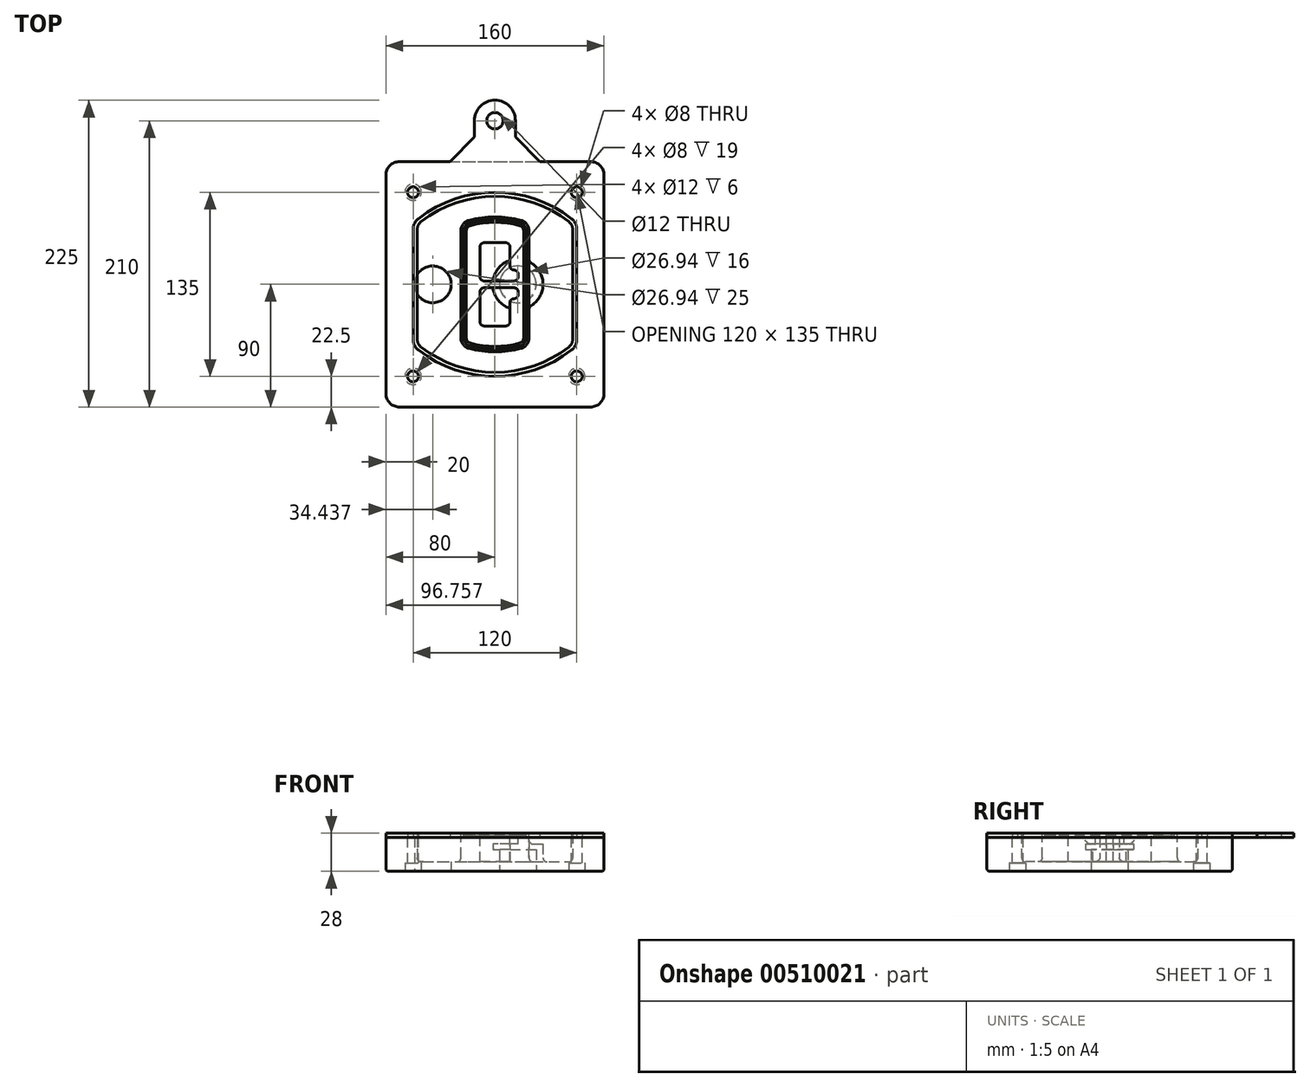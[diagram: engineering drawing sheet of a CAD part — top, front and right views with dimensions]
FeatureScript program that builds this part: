
annotation { "Feature Type Name" : "Feature", "Feature Type Description" : "" }
export const myFeature = defineFeature(function(context is Context, id is Id, definition is map)
    precondition{}
    {
        {
            var Q0;
            Q0=qCreatedBy(makeId("Top.planeOp"),FACE);
            var sketch = newSketch(context, id + "F0", { "sketchPlane" : qUnion([Q0])});
            skPoint(sketch, "E0.rect.middle", {"position": v(0, 0) * mm});
            skLineSegment(sketch, "E1.bottom", {"start": v(-70, -90) * mm, "end": v(70, -90) * mm});
            skLineSegment(sketch, "E1.top", {"start": v(-70, 90) * mm, "end": v(70, 90) * mm});
            skLineSegment(sketch, "E1.left", {"start": v(-80, -80) * mm, "end": v(-80, 80) * mm});
            skLineSegment(sketch, "E1.right", {"start": v(80, -80) * mm, "end": v(80, 80) * mm});
            skLineSegment(sketch, "E2", {"start": v(-80, 90) * mm, "end": v(80, -90) * mm, "construction": true});
            skLineSegment(sketch, "E3", {"start": v(80, 90) * mm, "end": v(-80, -90) * mm, "construction": true});
            skCircle(sketch, "E4", {"center": v(-60, 67.5) * mm, "radius": 4 * mm});
            skCircle(sketch, "E5", {"center": v(60, 67.5) * mm, "radius": 4 * mm});
            skCircle(sketch, "E6", {"center": v(60, -67.5) * mm, "radius": 4 * mm});
            skCircle(sketch, "E7", {"center": v(-60, -67.5) * mm, "radius": 4 * mm});
            skLineSegment(sketch, "E8", {"start": v(-60, 67.5) * mm, "end": v(60, 67.5) * mm, "construction": true});
            skLineSegment(sketch, "E9", {"start": v(60, 67.5) * mm, "end": v(60, -67.5) * mm, "construction": true});
            skLineSegment(sketch, "E10", {"start": v(60, -67.5) * mm, "end": v(-60, -67.5) * mm, "construction": true});
            skLineSegment(sketch, "E11", {"start": v(-60, -67.5) * mm, "end": v(-60, 67.5) * mm, "construction": true});
            skLineSegment(sketch, "E12", {"start": v(-60, 40.3) * mm, "end": v(-60, -40.3) * mm});
            skLineSegment(sketch, "E13", {"start": v(60, 40.3) * mm, "end": v(60, -40.3) * mm});
            skArc(sketch, "E14", {"start": v(56.15, 48.18) * mm, "mid": v(0, 67.5) * mm, "end": v(-56.15, 48.18) * mm});
            skArc(sketch, "E15", {"start": v(-56.15, -48.18) * mm, "mid": v(0, -67.5) * mm, "end": v(56.15, -48.18) * mm});
            skLineSegment(sketch, "E16", {"start": v(-60, 0) * mm, "end": v(60, 0) * mm, "construction": true});
            skPoint(sketch, "E17.visualSharp", {"position": v(-60, -45) * mm});
            skArc(sketch, "E17.filletArc", {"start": v(-60, -40.3) * mm, "mid": v(-58.99, -44.68) * mm, "end": v(-56.15, -48.18) * mm});
            skPoint(sketch, "E18.visualSharp", {"position": v(-60, 45) * mm});
            skArc(sketch, "E18.filletArc", {"start": v(-56.15, 48.18) * mm, "mid": v(-58.99, 44.68) * mm, "end": v(-60, 40.3) * mm});
            skPoint(sketch, "E19.visualSharp", {"position": v(60, 45) * mm});
            skArc(sketch, "E19.filletArc", {"start": v(60, 40.3) * mm, "mid": v(58.99, 44.68) * mm, "end": v(56.15, 48.18) * mm});
            skPoint(sketch, "E20.visualSharp", {"position": v(60, -45) * mm});
            skArc(sketch, "E20.filletArc", {"start": v(56.15, -48.18) * mm, "mid": v(58.99, -44.68) * mm, "end": v(60, -40.3) * mm});
            skPoint(sketch, "E21.visualSharp", {"position": v(-80, 90) * mm});
            skArc(sketch, "E21.filletArc", {"start": v(-70, 90) * mm, "mid": v(-77.07, 87.07) * mm, "end": v(-80, 80) * mm});
            skPoint(sketch, "E22.visualSharp", {"position": v(80, 90) * mm});
            skArc(sketch, "E22.filletArc", {"start": v(80, 80) * mm, "mid": v(77.07, 87.07) * mm, "end": v(70, 90) * mm});
            skPoint(sketch, "E23.visualSharp", {"position": v(80, -90) * mm});
            skArc(sketch, "E23.filletArc", {"start": v(70, -90) * mm, "mid": v(77.07, -87.07) * mm, "end": v(80, -80) * mm});
            skPoint(sketch, "E24.visualSharp", {"position": v(-80, -90) * mm});
            skArc(sketch, "E24.filletArc", {"start": v(-80, -80) * mm, "mid": v(-77.07, -87.07) * mm, "end": v(-70, -90) * mm});
            skArc(sketch, "E25.0", {"start": v(57, 40.3) * mm, "mid": v(56.3, 43.36) * mm, "end": v(54.3, 45.81) * mm});
            skLineSegment(sketch, "E25.1", {"start": v(57, 40.3) * mm, "end": v(57, -40.3) * mm});
            skArc(sketch, "E25.2", {"start": v(54.3, -45.81) * mm, "mid": v(56.3, -43.36) * mm, "end": v(57, -40.3) * mm});
            skArc(sketch, "E25.3", {"start": v(-54.3, -45.81) * mm, "mid": v(0, -64.5) * mm, "end": v(54.3, -45.81) * mm});
            skArc(sketch, "E25.4", {"start": v(-57, -40.3) * mm, "mid": v(-56.3, -43.36) * mm, "end": v(-54.3, -45.81) * mm});
            skArc(sketch, "E25.5", {"start": v(54.3, 45.81) * mm, "mid": v(0, 64.5) * mm, "end": v(-54.3, 45.81) * mm});
            skLineSegment(sketch, "E25.6", {"start": v(-57, 40.3) * mm, "end": v(-57, -40.3) * mm});
            skArc(sketch, "E25.7", {"start": v(-54.3, 45.81) * mm, "mid": v(-56.3, 43.36) * mm, "end": v(-57, 40.3) * mm});
            skArc(sketch, "E26.0", {"start": v(-58.62, 51.33) * mm, "mid": v(-62.58, 46.43) * mm, "end": v(-64, 40.3) * mm});
            skArc(sketch, "E26.1", {"start": v(58.62, 51.33) * mm, "mid": v(0, 71.5) * mm, "end": v(-58.62, 51.33) * mm});
            skArc(sketch, "E26.2", {"start": v(64, 40.3) * mm, "mid": v(62.58, 46.43) * mm, "end": v(58.62, 51.33) * mm});
            skLineSegment(sketch, "E26.3", {"start": v(64, 40.3) * mm, "end": v(64, -40.3) * mm});
            skArc(sketch, "E26.4", {"start": v(58.62, -51.33) * mm, "mid": v(62.58, -46.43) * mm, "end": v(64, -40.3) * mm});
            skLineSegment(sketch, "E26.5", {"start": v(-64, 40.3) * mm, "end": v(-64, -40.3) * mm});
            skArc(sketch, "E26.6", {"start": v(-58.62, -51.33) * mm, "mid": v(0, -71.5) * mm, "end": v(58.62, -51.33) * mm});
            skArc(sketch, "E26.7", {"start": v(-64, -40.3) * mm, "mid": v(-62.58, -46.43) * mm, "end": v(-58.62, -51.33) * mm});
            skSolve(sketch);
        }
        {
            var Q0;
            Q0=makeQuery(id+"F0.imprint","IMPRINT",FACE,{"disambiguationData":[TD([[makeQuery(id+"F0.imprint","IMPRINT",EDGE,{"derivedFrom":sQuery(id+"F0.wireOp",EDGE,"E1.bottom")}),1.0]])]});
            var Q1;
            Q1=makeQuery(id+"F0.imprint","IMPRINT",FACE,{"disambiguationData":[TD([[makeQuery(id+"F0.imprint","IMPRINT",EDGE,{"derivedFrom":sQuery(id+"F0.wireOp",EDGE,"E12")}),1.0]])]});
            var Q2;
            Q2=makeQuery(id+"F0.imprint","IMPRINT",FACE,{"disambiguationData":[TD([[makeQuery(id+"F0.imprint","IMPRINT",EDGE,{"derivedFrom":sQuery(id+"F0.wireOp",EDGE,"E25.0")}),1.0]])]});
            var Q3;
            Q3=makeQuery(id+"F0.imprint","IMPRINT",FACE,{"disambiguationData":[TD([[makeQuery(id+"F0.imprint","IMPRINT",EDGE,{"derivedFrom":sQuery(id+"F0.wireOp",EDGE,"E12")}),-1.0]])]});
            extrude(context, id + "F1", {"entities" : qUnion([Q0, Q1, Q2, Q3]), "oppositeDirection" : true, "depth" : 25 * mm});
        }
        {
            var Q0;
            Q0=makeQuery(id+"F0.imprint","IMPRINT",FACE,{"disambiguationData":[TD([[makeQuery(id+"F0.imprint","IMPRINT",EDGE,{"derivedFrom":sQuery(id+"F0.wireOp",EDGE,"E12")}),1.0]])]});
            extrude(context, id + "F2", {"entities" : qUnion([Q0]), "operationType" : NewBodyOperationType.ADD, "depth" : 3 * mm});
        }
        {
            var Q0;
            Q0=makeQuery(id+"F0.imprint","IMPRINT",FACE,{"disambiguationData":[TD([[makeQuery(id+"F0.imprint","IMPRINT",EDGE,{"derivedFrom":sQuery(id+"F0.wireOp",EDGE,"E25.0")}),1.0]])]});
            extrude(context, id + "F3", {"entities" : qUnion([Q0]), "operationType" : NewBodyOperationType.REMOVE, "oppositeDirection" : true, "depth" : 18 * mm});
        }
        {
            var Q0;
            Q0=makeQuery(id+"F2.opExtrude","CAP_FACE",FACE,{"disambiguationData":[OSD([sQuery(id+"F0.wireOp",EDGE,"E12"),sQuery(id+"F0.wireOp",EDGE,"E13"),sQuery(id+"F0.wireOp",EDGE,"E14"),sQuery(id+"F0.wireOp",EDGE,"E15"),sQuery(id+"F0.wireOp",EDGE,"E17.filletArc"),sQuery(id+"F0.wireOp",EDGE,"E18.filletArc"),sQuery(id+"F0.wireOp",EDGE,"E19.filletArc"),sQuery(id+"F0.wireOp",EDGE,"E20.filletArc"),sQuery(id+"F0.wireOp",EDGE,"E25.0"),sQuery(id+"F0.wireOp",EDGE,"E25.1"),sQuery(id+"F0.wireOp",EDGE,"E25.2"),sQuery(id+"F0.wireOp",EDGE,"E25.3"),sQuery(id+"F0.wireOp",EDGE,"E25.4"),sQuery(id+"F0.wireOp",EDGE,"E25.5"),sQuery(id+"F0.wireOp",EDGE,"E25.6"),sQuery(id+"F0.wireOp",EDGE,"E25.7")])],"isStart":false});
            var sketch = newSketch(context, id + "F4", { "sketchPlane" : qUnion([Q0])});
            skArc(sketch, "E27.0", {"start": v(-19.08, -46.97) * mm, "mid": v(0, -49.5) * mm, "end": v(19.08, -46.97) * mm});
            skArc(sketch, "E28.0", {"start": v(19.08, 46.97) * mm, "mid": v(0, 49.5) * mm, "end": v(-19.08, 46.97) * mm});
            skLineSegment(sketch, "E29", {"start": v(-25, 39.25) * mm, "end": v(-25, -39.25) * mm});
            skLineSegment(sketch, "E30", {"start": v(25, 39.25) * mm, "end": v(25, -39.25) * mm});
            skLineSegment(sketch, "E31", {"start": v(-25, 45.1) * mm, "end": v(25, 45.1) * mm, "construction": true});
            skLineSegment(sketch, "E32", {"start": v(-25, -45.1) * mm, "end": v(25, -45.1) * mm, "construction": true});
            skPoint(sketch, "E33.visualSharp", {"position": v(-25, 45.1) * mm});
            skArc(sketch, "E33.filletArc", {"start": v(-19.08, 46.97) * mm, "mid": v(-23.35, 44.11) * mm, "end": v(-25, 39.25) * mm});
            skPoint(sketch, "E34.visualSharp", {"position": v(25, 45.1) * mm});
            skArc(sketch, "E34.filletArc", {"start": v(25, 39.25) * mm, "mid": v(23.35, 44.11) * mm, "end": v(19.08, 46.97) * mm});
            skPoint(sketch, "E35.visualSharp", {"position": v(25, -45.1) * mm});
            skArc(sketch, "E35.filletArc", {"start": v(19.08, -46.97) * mm, "mid": v(23.35, -44.11) * mm, "end": v(25, -39.25) * mm});
            skPoint(sketch, "E36.visualSharp", {"position": v(-25, -45.1) * mm});
            skArc(sketch, "E36.filletArc", {"start": v(-25, -39.25) * mm, "mid": v(-23.35, -44.11) * mm, "end": v(-19.08, -46.97) * mm});
            skArc(sketch, "E37.0", {"start": v(54.3, 45.81) * mm, "mid": v(0, 64.5) * mm, "end": v(-54.3, 45.81) * mm});
            skArc(sketch, "E37.1", {"start": v(-54.3, 45.81) * mm, "mid": v(-56.3, 43.36) * mm, "end": v(-57, 40.3) * mm});
            skLineSegment(sketch, "E37.2", {"start": v(-57, 40.3) * mm, "end": v(-57, -40.3) * mm});
            skArc(sketch, "E37.3", {"start": v(-57, -40.3) * mm, "mid": v(-56.3, -43.36) * mm, "end": v(-54.3, -45.81) * mm});
            skArc(sketch, "E37.4", {"start": v(-54.3, -45.81) * mm, "mid": v(0, -64.5) * mm, "end": v(54.3, -45.81) * mm});
            skArc(sketch, "E37.5", {"start": v(54.3, -45.81) * mm, "mid": v(56.3, -43.36) * mm, "end": v(57, -40.3) * mm});
            skLineSegment(sketch, "E37.6", {"start": v(57, 40.3) * mm, "end": v(57, -40.3) * mm});
            skArc(sketch, "E37.7", {"start": v(57, 40.3) * mm, "mid": v(56.3, 43.36) * mm, "end": v(54.3, 45.81) * mm});
            skLineSegment(sketch, "E38.0", {"start": v(23, 39.25) * mm, "end": v(23, -39.25) * mm});
            skArc(sketch, "E38.1", {"start": v(18.56, -45.04) * mm, "mid": v(21.76, -42.9) * mm, "end": v(23, -39.25) * mm});
            skArc(sketch, "E38.2", {"start": v(-18.56, -45.04) * mm, "mid": v(0, -47.5) * mm, "end": v(18.56, -45.04) * mm});
            skArc(sketch, "E38.3", {"start": v(-23, -39.25) * mm, "mid": v(-21.76, -42.9) * mm, "end": v(-18.56, -45.04) * mm});
            skLineSegment(sketch, "E38.4", {"start": v(-23, 39.25) * mm, "end": v(-23, -39.25) * mm});
            skArc(sketch, "E38.5", {"start": v(23, 39.25) * mm, "mid": v(21.76, 42.9) * mm, "end": v(18.56, 45.04) * mm});
            skArc(sketch, "E38.6", {"start": v(-18.56, 45.04) * mm, "mid": v(-21.76, 42.9) * mm, "end": v(-23, 39.25) * mm});
            skArc(sketch, "E38.7", {"start": v(18.56, 45.04) * mm, "mid": v(0, 47.5) * mm, "end": v(-18.56, 45.04) * mm});
            skArc(sketch, "E39.0", {"start": v(21, 39.25) * mm, "mid": v(20.18, 41.68) * mm, "end": v(18.04, 43.1) * mm});
            skLineSegment(sketch, "E39.1", {"start": v(21, 39.25) * mm, "end": v(21, -39.25) * mm});
            skArc(sketch, "E39.2", {"start": v(18.04, -43.1) * mm, "mid": v(20.18, -41.68) * mm, "end": v(21, -39.25) * mm});
            skArc(sketch, "E39.3", {"start": v(-18.04, -43.1) * mm, "mid": v(0, -45.5) * mm, "end": v(18.04, -43.1) * mm});
            skArc(sketch, "E39.4", {"start": v(-21, -39.25) * mm, "mid": v(-20.18, -41.68) * mm, "end": v(-18.04, -43.1) * mm});
            skArc(sketch, "E39.5", {"start": v(18.04, 43.1) * mm, "mid": v(0, 45.5) * mm, "end": v(-18.04, 43.1) * mm});
            skLineSegment(sketch, "E39.6", {"start": v(-21, 39.25) * mm, "end": v(-21, -39.25) * mm});
            skArc(sketch, "E39.7", {"start": v(-18.04, 43.1) * mm, "mid": v(-20.18, 41.68) * mm, "end": v(-21, 39.25) * mm});
            skLineSegment(sketch, "E40", {"start": v(-25, 0) * mm, "end": v(25, 0) * mm, "construction": true});
            skLineSegment(sketch, "E41", {"start": v(-11, 5.5) * mm, "end": v(-11, 27.5) * mm});
            skLineSegment(sketch, "E42", {"start": v(-8, 30.5) * mm, "end": v(8, 30.5) * mm});
            skLineSegment(sketch, "E43", {"start": v(11, 27.5) * mm, "end": v(11, 13.5) * mm});
            skLineSegment(sketch, "E44", {"start": v(14, 10.5) * mm, "end": v(14, 10.5) * mm});
            skLineSegment(sketch, "E45", {"start": v(17, 7.5) * mm, "end": v(17, 5.5) * mm});
            skLineSegment(sketch, "E46", {"start": v(14, 2.5) * mm, "end": v(-8, 2.5) * mm});
            skPoint(sketch, "E47.visualSharp", {"position": v(-11, 30.5) * mm});
            skArc(sketch, "E47.filletArc", {"start": v(-8, 30.5) * mm, "mid": v(-10.12, 29.62) * mm, "end": v(-11, 27.5) * mm});
            skPoint(sketch, "E48.visualSharp", {"position": v(11, 30.5) * mm});
            skArc(sketch, "E48.filletArc", {"start": v(11, 27.5) * mm, "mid": v(10.12, 29.62) * mm, "end": v(8, 30.5) * mm});
            skPoint(sketch, "E49.visualSharp", {"position": v(11, 10.5) * mm});
            skArc(sketch, "E49.filletArc", {"start": v(11, 13.5) * mm, "mid": v(11.88, 11.38) * mm, "end": v(14, 10.5) * mm});
            skPoint(sketch, "E50.visualSharp", {"position": v(17, 10.5) * mm});
            skArc(sketch, "E50.filletArc", {"start": v(17, 7.5) * mm, "mid": v(16.12, 9.62) * mm, "end": v(14, 10.5) * mm});
            skPoint(sketch, "E51.visualSharp", {"position": v(17, 2.5) * mm});
            skArc(sketch, "E51.filletArc", {"start": v(14, 2.5) * mm, "mid": v(16.12, 3.38) * mm, "end": v(17, 5.5) * mm});
            skPoint(sketch, "E52.visualSharp", {"position": v(-11, 2.5) * mm});
            skArc(sketch, "E52.filletArc", {"start": v(-11, 5.5) * mm, "mid": v(-10.12, 3.38) * mm, "end": v(-8, 2.5) * mm});
            skLineSegment(sketch, "E53.0.MirrorCS", {"start": v(14, -2.5) * mm, "end": v(-8, -2.5) * mm});
            skArc(sketch, "E54.0.MirrorCS", {"start": v(-11, -5.5) * mm, "mid": v(-10.12, -3.38) * mm, "end": v(-8, -2.5) * mm});
            skLineSegment(sketch, "E55.0.MirrorCS", {"start": v(-11, -5.5) * mm, "end": v(-11, -27.5) * mm});
            skArc(sketch, "E56.0.MirrorCS", {"start": v(-8, -30.5) * mm, "mid": v(-10.12, -29.62) * mm, "end": v(-11, -27.5) * mm});
            skLineSegment(sketch, "E57.0.MirrorCS", {"start": v(-8, -30.5) * mm, "end": v(8, -30.5) * mm});
            skArc(sketch, "E58.0.MirrorCS", {"start": v(11, -27.5) * mm, "mid": v(10.12, -29.62) * mm, "end": v(8, -30.5) * mm});
            skLineSegment(sketch, "E59.0.MirrorCS", {"start": v(11, -27.5) * mm, "end": v(11, -13.5) * mm});
            skArc(sketch, "E60.0.MirrorCS", {"start": v(11, -13.5) * mm, "mid": v(11.88, -11.38) * mm, "end": v(14, -10.5) * mm});
            skArc(sketch, "E61.0.MirrorCS", {"start": v(17, -7.5) * mm, "mid": v(16.12, -9.62) * mm, "end": v(14, -10.5) * mm});
            skLineSegment(sketch, "E62.0.MirrorCS", {"start": v(17, -7.5) * mm, "end": v(17, -5.5) * mm});
            skArc(sketch, "E63.0.MirrorCS", {"start": v(14, -2.5) * mm, "mid": v(16.12, -3.38) * mm, "end": v(17, -5.5) * mm});
            skSolve(sketch);
        }
        {
            var Q0;
            Q0=makeQuery(id+"F4.imprint","IMPRINT",FACE,{"disambiguationData":[TD([[makeQuery(id+"F4.imprint","IMPRINT",EDGE,{"derivedFrom":sQuery(id+"F4.wireOp",EDGE,"E27.0")}),1.0]])]});
            var Q1;
            Q1=makeQuery(id+"F4.imprint","IMPRINT",FACE,{"disambiguationData":[TD([[makeQuery(id+"F4.imprint","IMPRINT",EDGE,{"derivedFrom":sQuery(id+"F4.wireOp",EDGE,"E38.0")}),-1.0]])]});
            var Q2;
            Q2=makeQuery(id+"F4.imprint","IMPRINT",FACE,{"disambiguationData":[TD([[makeQuery(id+"F4.imprint","IMPRINT",EDGE,{"derivedFrom":sQuery(id+"F4.wireOp",EDGE,"E39.0")}),1.0]])]});
            extrude(context, id + "F5", {"entities" : qUnion([Q0, Q1, Q2]), "operationType" : NewBodyOperationType.ADD, "endBound" : BoundingType.UP_TO_NEXT, "oppositeDirection" : true, "depth" : 25 * mm});
        }
        {
            var Q0;
            Q0=makeQuery(id+"F4.imprint","IMPRINT",FACE,{"disambiguationData":[TD([[makeQuery(id+"F4.imprint","IMPRINT",EDGE,{"derivedFrom":sQuery(id+"F4.wireOp",EDGE,"E38.0")}),-1.0]])]});
            extrude(context, id + "F6", {"entities" : qUnion([Q0]), "operationType" : NewBodyOperationType.REMOVE, "oppositeDirection" : true, "depth" : 2 * mm});
        }
        {
            var Q0;
            Q0=makeQuery(id+"F1.opExtrude","CAP_FACE",FACE,{"disambiguationData":[OSD([sQuery(id+"F0.wireOp",EDGE,"E1.bottom"),sQuery(id+"F0.wireOp",EDGE,"E1.top"),sQuery(id+"F0.wireOp",EDGE,"E1.left"),sQuery(id+"F0.wireOp",EDGE,"E1.right"),sQuery(id+"F0.wireOp",EDGE,"E4"),sQuery(id+"F0.wireOp",EDGE,"E5"),sQuery(id+"F0.wireOp",EDGE,"E6"),sQuery(id+"F0.wireOp",EDGE,"E7"),sQuery(id+"F0.wireOp",EDGE,"E21.filletArc"),sQuery(id+"F0.wireOp",EDGE,"E22.filletArc"),sQuery(id+"F0.wireOp",EDGE,"E23.filletArc"),sQuery(id+"F0.wireOp",EDGE,"E24.filletArc")])],"isStart":false});
            var sketch = newSketch(context, id + "F7", { "sketchPlane" : qUnion([Q0])});
            skCircle(sketch, "E64", {"center": v(16.76, 0) * mm, "radius": 13.47 * mm});
            skCircle(sketch, "E65", {"center": v(-45.56, 0) * mm, "radius": 13.47 * mm});
            skLineSegment(sketch, "E66", {"start": v(80, 0) * mm, "end": v(-80, 0) * mm});
            skCircle(sketch, "E67", {"center": v(16.76, 0) * mm, "radius": 18.47 * mm});
            skCircle(sketch, "E68", {"center": v(60, -67.5) * mm, "radius": 6 * mm});
            skCircle(sketch, "E69", {"center": v(-60, -67.5) * mm, "radius": 6 * mm});
            skCircle(sketch, "E70", {"center": v(-60, 67.5) * mm, "radius": 6 * mm});
            skCircle(sketch, "E71", {"center": v(60, 67.5) * mm, "radius": 6 * mm});
            skSolve(sketch);
        }
        {
            var Q0;
            {var subQ1=sQuery(id+"F7.wireOp",EDGE,"E66");var subQ4=sQuery(id+"F7.wireOp",EDGE,"E64");var subQ6=makeQuery(id+"F7.imprint","INTERSECT",VERTEX,{"disambiguationData":[OD(0.0)],"derivedFrom":[subQ4,subQ1]});Q0=makeQuery(id+"F7.imprint","IMPRINT",FACE,{"disambiguationData":[TD([[makeQuery(id+"F7.imprint","IMPRINT",EDGE,{"disambiguationData":[TD([[subQ6,-1.0]])],"derivedFrom":subQ4}),-1.0]])]});}
            var Q1;
            {var subQ0=sQuery(id+"F7.wireOp",EDGE,"E66");var subQ1=sQuery(id+"F7.wireOp",EDGE,"E64");var subQ3=makeQuery(id+"F7.imprint","INTERSECT",VERTEX,{"disambiguationData":[OD(0.0)],"derivedFrom":[subQ1,subQ0]});Q1=makeQuery(id+"F7.imprint","IMPRINT",FACE,{"disambiguationData":[TD([[makeQuery(id+"F7.imprint","IMPRINT",EDGE,{"disambiguationData":[TD([[subQ3,-1.0]])],"derivedFrom":subQ1}),1.0]])]});}
            var Q2;
            {var subQ0=sQuery(id+"F7.wireOp",EDGE,"E66");var subQ1=sQuery(id+"F7.wireOp",EDGE,"E64");var subQ3=makeQuery(id+"F7.imprint","INTERSECT",VERTEX,{"disambiguationData":[OD(0.0)],"derivedFrom":[subQ1,subQ0]});Q2=makeQuery(id+"F7.imprint","IMPRINT",FACE,{"disambiguationData":[TD([[makeQuery(id+"F7.imprint","IMPRINT",EDGE,{"disambiguationData":[TD([[subQ3,1.0]])],"derivedFrom":subQ1}),1.0]])]});}
            var Q3;
            {var subQ1=sQuery(id+"F7.wireOp",EDGE,"E66");var subQ4=sQuery(id+"F7.wireOp",EDGE,"E64");var subQ6=makeQuery(id+"F7.imprint","INTERSECT",VERTEX,{"disambiguationData":[OD(0.0)],"derivedFrom":[subQ4,subQ1]});Q3=makeQuery(id+"F7.imprint","IMPRINT",FACE,{"disambiguationData":[TD([[makeQuery(id+"F7.imprint","IMPRINT",EDGE,{"disambiguationData":[TD([[subQ6,1.0]])],"derivedFrom":subQ4}),-1.0]])]});}
            extrude(context, id + "F8", {"entities" : qUnion([Q0, Q1, Q2, Q3]), "operationType" : NewBodyOperationType.ADD, "oppositeDirection" : true, "depth" : 20 * mm});
        }
        {
            var Q0;
            {var subQ0=sQuery(id+"F7.wireOp",EDGE,"E66");var subQ1=sQuery(id+"F7.wireOp",EDGE,"E64");var subQ3=makeQuery(id+"F7.imprint","INTERSECT",VERTEX,{"disambiguationData":[OD(0.0)],"derivedFrom":[subQ1,subQ0]});Q0=makeQuery(id+"F7.imprint","IMPRINT",FACE,{"disambiguationData":[TD([[makeQuery(id+"F7.imprint","IMPRINT",EDGE,{"disambiguationData":[TD([[subQ3,-1.0]])],"derivedFrom":subQ1}),1.0]])]});}
            var Q1;
            {var subQ0=sQuery(id+"F7.wireOp",EDGE,"E66");var subQ1=sQuery(id+"F7.wireOp",EDGE,"E64");var subQ3=makeQuery(id+"F7.imprint","INTERSECT",VERTEX,{"disambiguationData":[OD(0.0)],"derivedFrom":[subQ1,subQ0]});Q1=makeQuery(id+"F7.imprint","IMPRINT",FACE,{"disambiguationData":[TD([[makeQuery(id+"F7.imprint","IMPRINT",EDGE,{"disambiguationData":[TD([[subQ3,1.0]])],"derivedFrom":subQ1}),1.0]])]});}
            extrude(context, id + "F9", {"entities" : qUnion([Q0, Q1]), "operationType" : NewBodyOperationType.REMOVE, "oppositeDirection" : true, "depth" : 16 * mm});
        }
        {
            var Q0;
            {var subQ0=sQuery(id+"F7.wireOp",EDGE,"E66");var subQ1=sQuery(id+"F7.wireOp",EDGE,"E65");var subQ3=makeQuery(id+"F7.imprint","INTERSECT",VERTEX,{"disambiguationData":[OD(0.0)],"derivedFrom":[subQ1,subQ0]});Q0=makeQuery(id+"F7.imprint","IMPRINT",FACE,{"disambiguationData":[TD([[makeQuery(id+"F7.imprint","IMPRINT",EDGE,{"disambiguationData":[TD([[subQ3,-1.0]])],"derivedFrom":subQ1}),1.0]])]});}
            var Q1;
            {var subQ0=sQuery(id+"F7.wireOp",EDGE,"E66");var subQ1=sQuery(id+"F7.wireOp",EDGE,"E65");var subQ3=makeQuery(id+"F7.imprint","INTERSECT",VERTEX,{"disambiguationData":[OD(0.0)],"derivedFrom":[subQ1,subQ0]});Q1=makeQuery(id+"F7.imprint","IMPRINT",FACE,{"disambiguationData":[TD([[makeQuery(id+"F7.imprint","IMPRINT",EDGE,{"disambiguationData":[TD([[subQ3,1.0]])],"derivedFrom":subQ1}),1.0]])]});}
            extrude(context, id + "F10", {"entities" : qUnion([Q0, Q1]), "operationType" : NewBodyOperationType.REMOVE, "oppositeDirection" : true, "depth" : 25 * mm});
        }
        {
            var Q0;
            Q0=makeQuery(id+"F7.imprint","IMPRINT",FACE,{"disambiguationData":[TD([[makeQuery(id+"F7.imprint","IMPRINT",EDGE,{"derivedFrom":sQuery(id+"F7.wireOp",EDGE,"E68")}),1.0]])]});
            var Q1;
            Q1=makeQuery(id+"F7.imprint","IMPRINT",FACE,{"disambiguationData":[TD([[makeQuery(id+"F7.imprint","IMPRINT",EDGE,{"derivedFrom":makeQuery(id+"F1.opExtrude","CAP_EDGE",EDGE,{"disambiguationData":[OSD([sQuery(id+"F0.wireOp",EDGE,"E5")])],"isStart":false})}),-1.0]])]});
            var Q2;
            Q2=makeQuery(id+"F7.imprint","IMPRINT",FACE,{"disambiguationData":[TD([[makeQuery(id+"F7.imprint","IMPRINT",EDGE,{"derivedFrom":sQuery(id+"F7.wireOp",EDGE,"E69")}),1.0]])]});
            var Q3;
            Q3=makeQuery(id+"F7.imprint","IMPRINT",FACE,{"disambiguationData":[TD([[makeQuery(id+"F7.imprint","IMPRINT",EDGE,{"derivedFrom":makeQuery(id+"F1.opExtrude","CAP_EDGE",EDGE,{"disambiguationData":[OSD([sQuery(id+"F0.wireOp",EDGE,"E4")])],"isStart":false})}),-1.0]])]});
            var Q4;
            Q4=makeQuery(id+"F7.imprint","IMPRINT",FACE,{"disambiguationData":[TD([[makeQuery(id+"F7.imprint","IMPRINT",EDGE,{"derivedFrom":sQuery(id+"F7.wireOp",EDGE,"E70")}),1.0]])]});
            var Q5;
            Q5=makeQuery(id+"F7.imprint","IMPRINT",FACE,{"disambiguationData":[TD([[makeQuery(id+"F7.imprint","IMPRINT",EDGE,{"derivedFrom":makeQuery(id+"F1.opExtrude","CAP_EDGE",EDGE,{"disambiguationData":[OSD([sQuery(id+"F0.wireOp",EDGE,"E7")])],"isStart":false})}),-1.0]])]});
            var Q6;
            Q6=makeQuery(id+"F7.imprint","IMPRINT",FACE,{"disambiguationData":[TD([[makeQuery(id+"F7.imprint","IMPRINT",EDGE,{"derivedFrom":sQuery(id+"F7.wireOp",EDGE,"E71")}),1.0]])]});
            var Q7;
            Q7=makeQuery(id+"F7.imprint","IMPRINT",FACE,{"disambiguationData":[TD([[makeQuery(id+"F7.imprint","IMPRINT",EDGE,{"derivedFrom":makeQuery(id+"F1.opExtrude","CAP_EDGE",EDGE,{"disambiguationData":[OSD([sQuery(id+"F0.wireOp",EDGE,"E6")])],"isStart":false})}),-1.0]])]});
            extrude(context, id + "F11", {"entities" : qUnion([Q0, Q1, Q2, Q3, Q4, Q5, Q6, Q7]), "operationType" : NewBodyOperationType.REMOVE, "oppositeDirection" : true, "depth" : 6 * mm});
        }
        {
            var Q0;
            Q0=makeQuery(id+"F9.boolean.opBoolean","COPY",FACE,{"derivedFrom":makeQuery(id+"F9.opExtrude","CAP_FACE",FACE,{"disambiguationData":[OSD([sQuery(id+"F7.wireOp",EDGE,"E64")])],"isStart":false})});
            var sketch = newSketch(context, id + "F12", { "sketchPlane" : qUnion([Q0])});
            skArc(sketch, "E72.0", {"start": v(11, 17.55) * mm, "mid": v(2.57, 11.82) * mm, "end": v(-1.54, 2.5) * mm});
            skArc(sketch, "E72.1", {"start": v(-1.54, -2.5) * mm, "mid": v(2.57, -11.82) * mm, "end": v(11, -17.55) * mm});
            skLineSegment(sketch, "E73", {"start": v(-1.54, -2.5) * mm, "end": v(14, -2.5) * mm});
            skLineSegment(sketch, "E74.0", {"start": v(14, 2.5) * mm, "end": v(-1.54, 2.5) * mm});
            skArc(sketch, "E74.1", {"start": v(14, 2.5) * mm, "mid": v(16.12, 3.38) * mm, "end": v(17, 5.5) * mm});
            skLineSegment(sketch, "E74.2", {"start": v(17, 7.5) * mm, "end": v(17, 5.5) * mm});
            skArc(sketch, "E74.3", {"start": v(17, 7.5) * mm, "mid": v(16.12, 9.62) * mm, "end": v(14, 10.5) * mm});
            skArc(sketch, "E74.4", {"start": v(11, 13.5) * mm, "mid": v(11.88, 11.38) * mm, "end": v(14, 10.5) * mm});
            skLineSegment(sketch, "E74.5", {"start": v(11, 17.55) * mm, "end": v(11, 13.5) * mm});
            skLineSegment(sketch, "E74.7", {"start": v(14, -2.5) * mm, "end": v(-1.54, -2.5) * mm});
            skArc(sketch, "E74.8", {"start": v(14, -2.5) * mm, "mid": v(16.12, -3.38) * mm, "end": v(17, -5.5) * mm});
            skLineSegment(sketch, "E74.9", {"start": v(17, -7.5) * mm, "end": v(17, -5.5) * mm});
            skArc(sketch, "E74.10", {"start": v(17, -7.5) * mm, "mid": v(16.12, -9.62) * mm, "end": v(14, -10.5) * mm});
            skArc(sketch, "E74.11", {"start": v(11, -13.5) * mm, "mid": v(11.88, -11.38) * mm, "end": v(14, -10.5) * mm});
            skLineSegment(sketch, "E74.12", {"start": v(11, -17.55) * mm, "end": v(11, -13.5) * mm});
            skPoint(sketch, "E75.orphan", {"position": v(11, -27.5) * mm});
            skPoint(sketch, "E76.orphan", {"position": v(-8, -2.5) * mm});
            skPoint(sketch, "E77.orphan", {"position": v(-8, 2.5) * mm});
            skPoint(sketch, "E78.orphan", {"position": v(11, 27.5) * mm});
            skSolve(sketch);
        }
        {
            var Q0;
            {var subQ7=sQuery(id+"F12.wireOp",EDGE,"E72.0");var subQ14=sQuery(id+"F12.wireOp",EDGE,"E72.1");var subQ16=sQuery(id+"F12.wireOp",EDGE,"E74.1");var subQ18=sQuery(id+"F12.wireOp",EDGE,"E74.8");Q0=qUnion([makeQuery(id+"F12.imprint","IMPRINT",FACE,{"disambiguationData":[TD([[makeQuery(id+"F12.imprint","IMPRINT",EDGE,{"derivedFrom":subQ7}),1.0]])]}),makeQuery(id+"F12.imprint","IMPRINT",FACE,{"disambiguationData":[TD([[makeQuery(id+"F12.imprint","IMPRINT",EDGE,{"derivedFrom":subQ14}),1.0]])]}),makeQuery(id+"F12.imprint","IMPRINT",FACE,{"disambiguationData":[TD([[makeQuery(id+"F12.imprint","IMPRINT",EDGE,{"derivedFrom":subQ16}),1.0]])]}),makeQuery(id+"F12.imprint","IMPRINT",FACE,{"disambiguationData":[TD([[makeQuery(id+"F12.imprint","IMPRINT",EDGE,{"derivedFrom":subQ18}),-1.0]])]})]);}
            var Q1;
            Q1=makeQuery(id+"F5.boolean.opBoolean","SPLIT",FACE,{"disambiguationData":[TD([makeQuery(id+"F5.opExtrude","SWEPT_FACE",FACE,{"disambiguationData":[OSD([sQuery(id+"F4.wireOp",EDGE,"E41")])]})])],"derivedFrom":makeQuery(id+"F3.boolean.opBoolean","COPY",FACE,{"derivedFrom":makeQuery(id+"F3.opExtrude","CAP_FACE",FACE,{"disambiguationData":[OSD([sQuery(id+"F0.wireOp",EDGE,"E25.0"),sQuery(id+"F0.wireOp",EDGE,"E25.1"),sQuery(id+"F0.wireOp",EDGE,"E25.2"),sQuery(id+"F0.wireOp",EDGE,"E25.3"),sQuery(id+"F0.wireOp",EDGE,"E25.4"),sQuery(id+"F0.wireOp",EDGE,"E25.5"),sQuery(id+"F0.wireOp",EDGE,"E25.6"),sQuery(id+"F0.wireOp",EDGE,"E25.7")])],"isStart":false})})});
            extrude(context, id + "F13", {"entities" : qUnion([Q0]), "operationType" : NewBodyOperationType.REMOVE, "endBound" : BoundingType.UP_TO_SURFACE, "endBoundEntityFace" : qUnion([Q1]), "depth" : 25 * mm});
        }
        {
            var Q0;
            Q0=makeQuery(id+"F3.boolean.opBoolean","COPY",EDGE,{"derivedFrom":makeQuery(id+"F3.opExtrude","CAP_EDGE",EDGE,{"disambiguationData":[OSD([sQuery(id+"F0.wireOp",EDGE,"E25.6")])],"isStart":false})});
            var Q1;
            Q1=makeQuery(id+"F8.boolean.opBoolean","INTERSECT",EDGE,{"derivedFrom":[makeQuery(id+"F5.opExtrude","SWEPT_FACE",FACE,{"disambiguationData":[OSD([sQuery(id+"F4.wireOp",EDGE,"E30")])]}),makeQuery(id+"F8.opExtrude","CAP_FACE",FACE,{"disambiguationData":[OSD([sQuery(id+"F7.wireOp",EDGE,"E67")])],"isStart":false})]});
            var Q2;
            Q2=makeQuery(id+"F8.boolean.opBoolean","INTERSECT",EDGE,{"disambiguationData":[OD(1.0)],"derivedFrom":[makeQuery(id+"F5.opExtrude","SWEPT_FACE",FACE,{"disambiguationData":[OSD([sQuery(id+"F4.wireOp",EDGE,"E30")])]}),makeQuery(id+"F8.opExtrude","SWEPT_FACE",FACE,{"disambiguationData":[OSD([sQuery(id+"F7.wireOp",EDGE,"E67")])]})]});
            var Q3;
            {var subQ0=sQuery(id+"F4.wireOp",EDGE,"E30");Q3=makeQuery(id+"F8.boolean.opBoolean","SPLIT",EDGE,{"disambiguationData":[TD([makeQuery(id+"F5.opExtrude","SWEPT_FACE",FACE,{"disambiguationData":[OSD([sQuery(id+"F4.wireOp",EDGE,"E35.filletArc")])]})])],"derivedFrom":makeQuery(id+"F5.opExtrude","CAP_EDGE",EDGE,{"disambiguationData":[OSD([subQ0])],"isStart":false})});}
            var Q4;
            {var subQ0=sQuery(id+"F0.wireOp",EDGE,"E25.7");var subQ1=sQuery(id+"F0.wireOp",EDGE,"E25.1");var subQ2=sQuery(id+"F0.wireOp",EDGE,"E25.6");var subQ3=sQuery(id+"F0.wireOp",EDGE,"E25.5");var subQ4=sQuery(id+"F0.wireOp",EDGE,"E25.4");var subQ5=sQuery(id+"F0.wireOp",EDGE,"E25.0");var subQ6=sQuery(id+"F0.wireOp",EDGE,"E25.2");var subQ7=sQuery(id+"F0.wireOp",EDGE,"E25.3");Q4=makeQuery(id+"F8.boolean.opBoolean","INTERSECT",EDGE,{"derivedFrom":[makeQuery(id+"F5.boolean.opBoolean","SPLIT",FACE,{"disambiguationData":[TD([makeQuery(id+"F2.opExtrude","SWEPT_FACE",FACE,{"disambiguationData":[OSD([subQ5])]})])],"derivedFrom":makeQuery(id+"F3.boolean.opBoolean","COPY",FACE,{"derivedFrom":makeQuery(id+"F3.opExtrude","CAP_FACE",FACE,{"disambiguationData":[OSD([subQ5,subQ1,subQ6,subQ7,subQ4,subQ3,subQ2,subQ0])],"isStart":false})})}),makeQuery(id+"F8.opExtrude","SWEPT_FACE",FACE,{"disambiguationData":[OSD([sQuery(id+"F7.wireOp",EDGE,"E67")])]})]});}
            var Q5;
            Q5=makeQuery(id+"F8.boolean.opBoolean","INTERSECT",EDGE,{"disambiguationData":[OD(0.0)],"derivedFrom":[makeQuery(id+"F5.opExtrude","SWEPT_FACE",FACE,{"disambiguationData":[OSD([sQuery(id+"F4.wireOp",EDGE,"E30")])]}),makeQuery(id+"F8.opExtrude","SWEPT_FACE",FACE,{"disambiguationData":[OSD([sQuery(id+"F7.wireOp",EDGE,"E67")])]})]});
            fillet(context, id + "F14", {"entities" : qUnion([Q0, Q1, Q2, Q3, Q4, Q5]), "radius" : 3 * mm, "tangentPropagation" : true, "allowEdgeOverflow" : false});
        }
        {
            var Q0;
            Q0=makeQuery(id+"F1.opExtrude","CAP_EDGE",EDGE,{"disambiguationData":[OSD([sQuery(id+"F0.wireOp",EDGE,"E1.bottom")])],"isStart":false});
            fillet(context, id + "F15", {"entities" : qUnion([Q0]), "radius" : 2 * mm, "tangentPropagation" : true, "allowEdgeOverflow" : false});
        }
        {
            var Q0;
            {var subQ0=sQuery(id+"F0.wireOp",EDGE,"E21.filletArc");var subQ1=sQuery(id+"F0.wireOp",EDGE,"E7");var subQ2=sQuery(id+"F0.wireOp",EDGE,"E6");var subQ3=sQuery(id+"F0.wireOp",EDGE,"E5");var subQ4=sQuery(id+"F0.wireOp",EDGE,"E4");var subQ5=sQuery(id+"F0.wireOp",EDGE,"E22.filletArc");var subQ6=sQuery(id+"F0.wireOp",EDGE,"E1.bottom");var subQ7=sQuery(id+"F0.wireOp",EDGE,"E1.right");var subQ8=sQuery(id+"F0.wireOp",EDGE,"E1.top");var subQ9=sQuery(id+"F0.wireOp",EDGE,"E1.left");var subQ10=sQuery(id+"F0.wireOp",EDGE,"E23.filletArc");var subQ11=sQuery(id+"F0.wireOp",EDGE,"E24.filletArc");Q0=makeQuery(id+"F2.boolean.opBoolean","SPLIT",FACE,{"disambiguationData":[TD([makeQuery(id+"F1.opExtrude","SWEPT_FACE",FACE,{"disambiguationData":[OSD([subQ6])]})])],"derivedFrom":makeQuery(id+"F1.opExtrude","CAP_FACE",FACE,{"disambiguationData":[OSD([subQ6,subQ8,subQ9,subQ7,subQ4,subQ3,subQ2,subQ1,subQ0,subQ5,subQ10,subQ11])],"isStart":true})});}
            var sketch = newSketch(context, id + "F16", { "sketchPlane" : qUnion([Q0])});
            skLineSegment(sketch, "E79", {"start": v(0, 90) * mm, "end": v(0, 98.25) * mm, "construction": true});
            skLineSegment(sketch, "E80", {"start": v(-33, 90) * mm, "end": v(-15, 108) * mm});
            skLineSegment(sketch, "E81", {"start": v(-15, 108) * mm, "end": v(-15, 120) * mm});
            skLineSegment(sketch, "E82", {"start": v(33, 90) * mm, "end": v(15, 108) * mm});
            skLineSegment(sketch, "E83", {"start": v(15, 108) * mm, "end": v(15, 120) * mm});
            skArc(sketch, "E84", {"start": v(15, 120) * mm, "mid": v(0, 135) * mm, "end": v(-15, 120) * mm});
            skLineSegment(sketch, "E85", {"start": v(-80, 0) * mm, "end": v(80, 0) * mm, "construction": true});
            skArc(sketch, "E86.MirrorCS", {"start": v(15, -120) * mm, "mid": v(0, -135) * mm, "end": v(-15, -120) * mm});
            skLineSegment(sketch, "E87.MirrorCS", {"start": v(-15, -108) * mm, "end": v(-15, -120) * mm});
            skLineSegment(sketch, "E88.MirrorCS", {"start": v(-33, -90) * mm, "end": v(-15, -108) * mm});
            skLineSegment(sketch, "E89.MirrorCS", {"start": v(33, -90) * mm, "end": v(15, -108) * mm});
            skLineSegment(sketch, "E90.MirrorCS", {"start": v(15, -108) * mm, "end": v(15, -120) * mm});
            skLineSegment(sketch, "E91.MirrorCS", {"start": v(0, -90) * mm, "end": v(0, -98.25) * mm, "construction": true});
            skCircle(sketch, "E92", {"center": v(0, 120) * mm, "radius": 6 * mm});
            skCircle(sketch, "E93", {"center": v(0, -120) * mm, "radius": 6 * mm});
            skSolve(sketch);
        }
        {
            var Q0;
            Q0=makeQuery(id+"F16.imprint","IMPRINT",FACE,{"disambiguationData":[TD([[makeQuery(id+"F16.imprint","IMPRINT",EDGE,{"derivedFrom":sQuery(id+"F16.wireOp",EDGE,"E86.MirrorCS")}),-1.0]])]});
            var Q1;
            {var subQ1=sQuery(id+"F16.wireOp",EDGE,"E80");Q1=makeQuery(id+"F16.imprint","IMPRINT",FACE,{"disambiguationData":[TD([[makeQuery(id+"F16.imprint","IMPRINT",EDGE,{"derivedFrom":subQ1}),-1.0]])]});}
            var Q2;
            Q2=makeQuery(id+"F16.imprint","IMPRINT",FACE,{"disambiguationData":[TD([[makeQuery(id+"F16.imprint","IMPRINT",EDGE,{"derivedFrom":makeQuery(id+"F1.opExtrude","CAP_EDGE",EDGE,{"disambiguationData":[OSD([sQuery(id+"F0.wireOp",EDGE,"E1.left")])],"isStart":true})}),-1.0]])]});
            var Q3;
            Q3=makeQuery(id+"F2.opExtrude","CAP_FACE",FACE,{"disambiguationData":[OSD([sQuery(id+"F0.wireOp",EDGE,"E12"),sQuery(id+"F0.wireOp",EDGE,"E13"),sQuery(id+"F0.wireOp",EDGE,"E14"),sQuery(id+"F0.wireOp",EDGE,"E15"),sQuery(id+"F0.wireOp",EDGE,"E17.filletArc"),sQuery(id+"F0.wireOp",EDGE,"E18.filletArc"),sQuery(id+"F0.wireOp",EDGE,"E19.filletArc"),sQuery(id+"F0.wireOp",EDGE,"E20.filletArc"),sQuery(id+"F0.wireOp",EDGE,"E25.0"),sQuery(id+"F0.wireOp",EDGE,"E25.1"),sQuery(id+"F0.wireOp",EDGE,"E25.2"),sQuery(id+"F0.wireOp",EDGE,"E25.3"),sQuery(id+"F0.wireOp",EDGE,"E25.4"),sQuery(id+"F0.wireOp",EDGE,"E25.5"),sQuery(id+"F0.wireOp",EDGE,"E25.6"),sQuery(id+"F0.wireOp",EDGE,"E25.7")])],"isStart":false});
            extrude(context, id + "F17", {"entities" : qUnion([Q0, Q1, Q2]), "endBound" : BoundingType.UP_TO_SURFACE, "depth" : 25 * mm, "endBoundEntityFace" : qUnion([Q3]), "offsetDistance" : 25 * mm});
        }
    });
